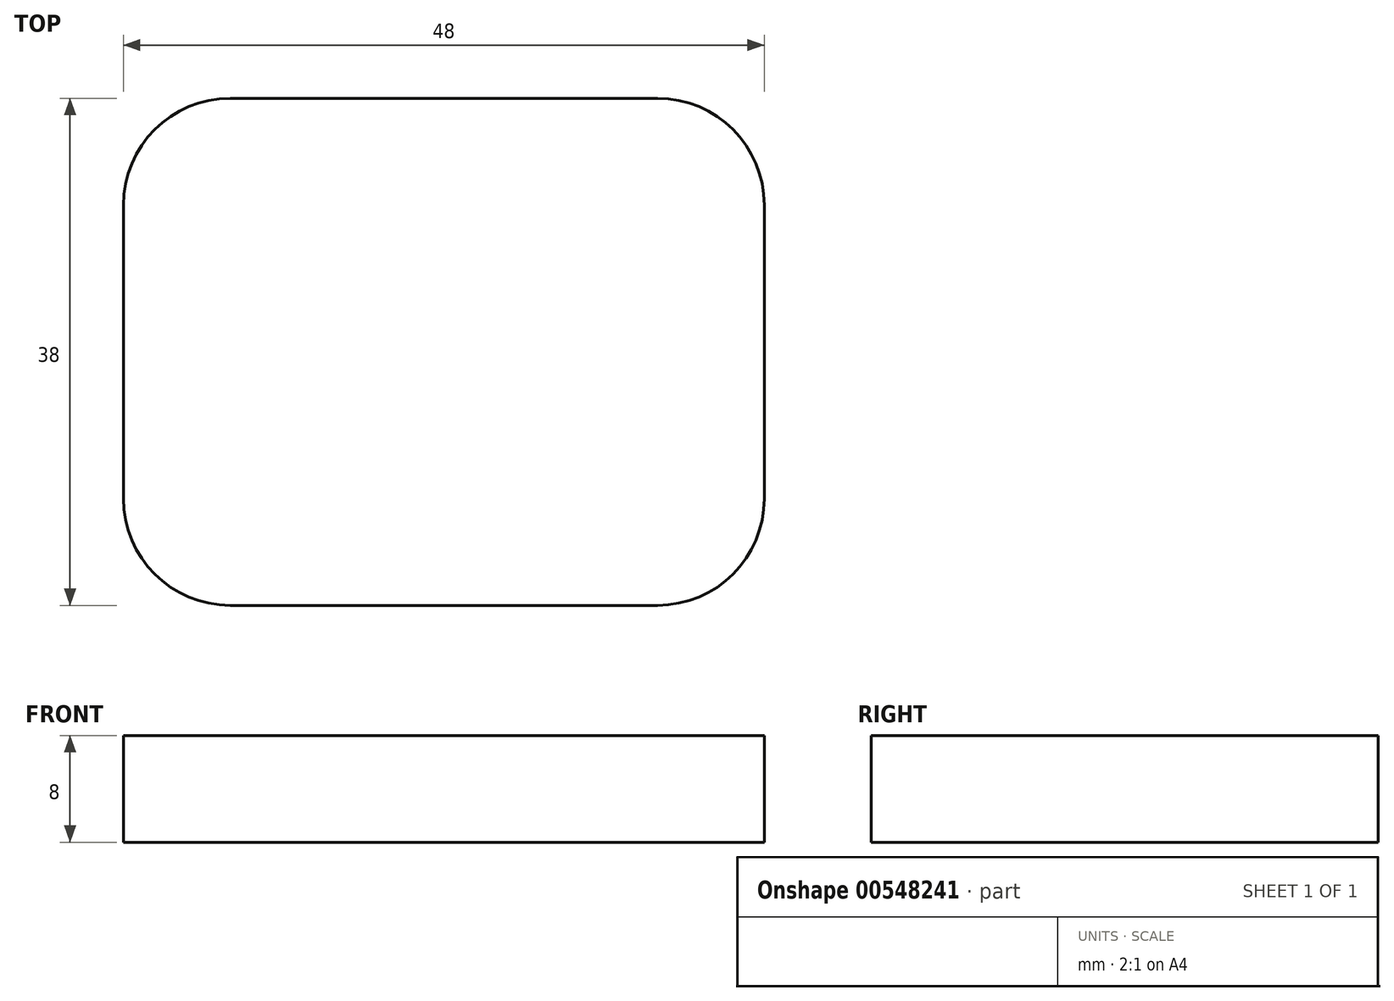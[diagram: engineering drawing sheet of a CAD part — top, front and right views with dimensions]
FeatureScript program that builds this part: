
annotation { "Feature Type Name" : "Feature", "Feature Type Description" : "" }
export const myFeature = defineFeature(function(context is Context, id is Id, definition is map)
    precondition{}
    {
        {
            var Q0;
            Q0=qCreatedBy(makeId("Top.planeOp"),FACE);
            var sketch = newSketch(context, id + "F0", { "sketchPlane" : qUnion([Q0])});
            skLineSegment(sketch, "E0.bottom", {"start": v(-1165.91, 8.2) * mm, "end": v(-1117.91, 8.2) * mm});
            skLineSegment(sketch, "E0.top", {"start": v(-1165.91, -29.8) * mm, "end": v(-1117.91, -29.8) * mm});
            skLineSegment(sketch, "E0.left", {"start": v(-1165.91, 8.2) * mm, "end": v(-1165.91, -29.8) * mm});
            skLineSegment(sketch, "E0.right", {"start": v(-1117.91, 8.2) * mm, "end": v(-1117.91, -29.8) * mm});
            skLineSegment(sketch, "E1.bottom", {"start": v(-16, 19) * mm, "end": v(16, 19) * mm});
            skLineSegment(sketch, "E1.top", {"start": v(-16, -19) * mm, "end": v(16, -19) * mm});
            skLineSegment(sketch, "E1.left", {"start": v(-24, 11) * mm, "end": v(-24, -11) * mm});
            skLineSegment(sketch, "E1.right", {"start": v(24, 11) * mm, "end": v(24, -11) * mm});
            skPoint(sketch, "E2.visualSharp", {"position": v(-24, 19) * mm});
            skArc(sketch, "E2.filletArc", {"start": v(-16, 19) * mm, "mid": v(-21.66, 16.66) * mm, "end": v(-24, 11) * mm});
            skPoint(sketch, "E3.visualSharp", {"position": v(24, 19) * mm});
            skArc(sketch, "E3.filletArc", {"start": v(24, 11) * mm, "mid": v(21.66, 16.66) * mm, "end": v(16, 19) * mm});
            skPoint(sketch, "E4.visualSharp", {"position": v(24, -19) * mm});
            skArc(sketch, "E4.filletArc", {"start": v(16, -19) * mm, "mid": v(21.66, -16.66) * mm, "end": v(24, -11) * mm});
            skPoint(sketch, "E5.visualSharp", {"position": v(-24, -19) * mm});
            skArc(sketch, "E5.filletArc", {"start": v(-24, -11) * mm, "mid": v(-21.66, -16.66) * mm, "end": v(-16, -19) * mm});
            skSolve(sketch);
        }
        {
            var Q0;
            Q0=makeQuery(id+"F0.imprint","IMPRINT",FACE,{"disambiguationData":[TD([[makeQuery(id+"F0.imprint","IMPRINT",EDGE,{"derivedFrom":sQuery(id+"F0.wireOp",EDGE,"E1.bottom")}),-1.0]])]});
            extrude(context, id + "F1", {"entities" : qUnion([Q0]), "depth" : 8 * mm, "offsetDistance" : 25 * mm});
        }
    });
